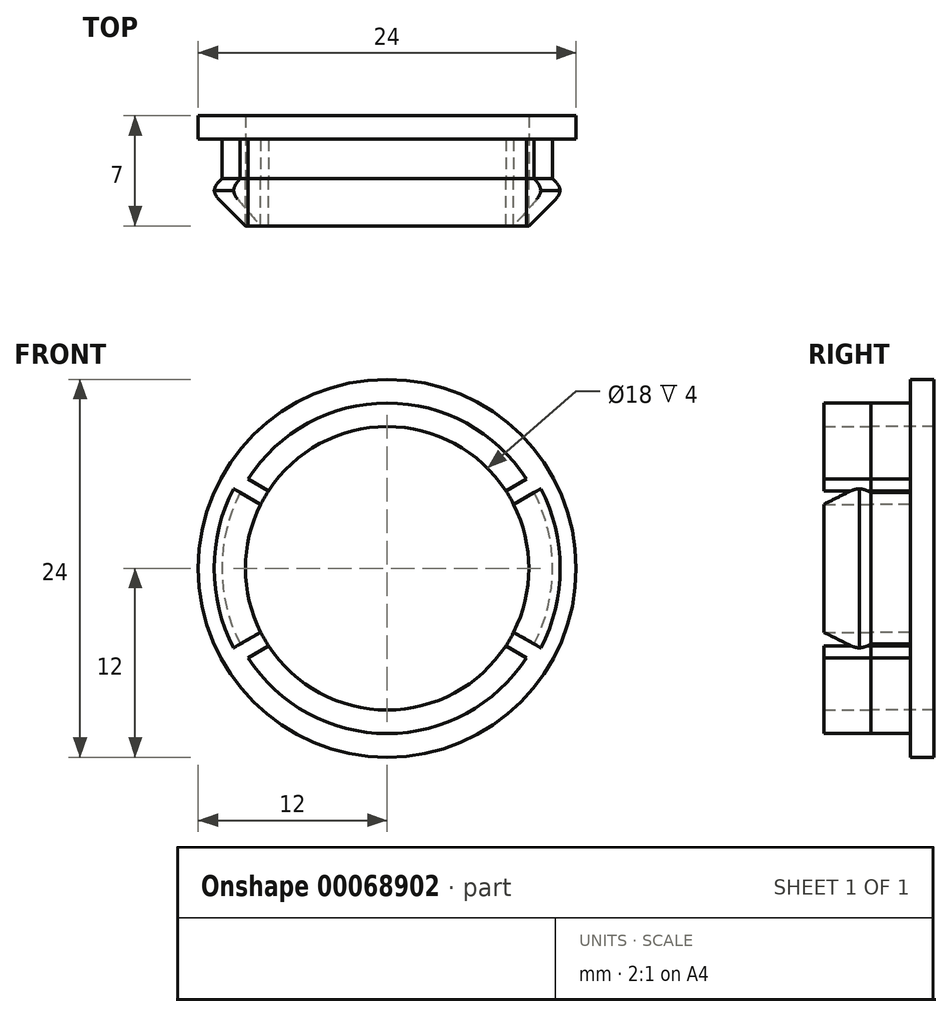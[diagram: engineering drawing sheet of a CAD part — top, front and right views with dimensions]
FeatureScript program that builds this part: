
annotation { "Feature Type Name" : "Feature", "Feature Type Description" : "" }
export const myFeature = defineFeature(function(context is Context, id is Id, definition is map)
    precondition{}
    {
        {
            var Q0;
            Q0=qCreatedBy(makeId("Front.planeOp"),FACE);
            var sketch = newSketch(context, id + "F0", { "sketchPlane" : qUnion([Q0])});
            skArc(sketch, "E0", {"start": v(-9.33, 4.81) * mm, "mid": v(-10.5, 0) * mm, "end": v(-9.33, -4.81) * mm});
            skArc(sketch, "E1.0", {"start": v(-8.03, 4.06) * mm, "mid": v(-9, 0) * mm, "end": v(-8.03, -4.06) * mm});
            skLineSegment(sketch, "E2", {"start": v(-12.74, 7.35) * mm, "end": v(0, 0) * mm, "construction": true});
            skLineSegment(sketch, "E3.MirrorCS", {"start": v(-12.74, -7.35) * mm, "end": v(0, 0) * mm, "construction": true});
            skLineSegment(sketch, "E4.0", {"start": v(-12.88, -6.86) * mm, "end": v(-1, 0) * mm});
            skLineSegment(sketch, "E4.1", {"start": v(-9.33, 4.81) * mm, "end": v(-1, 0) * mm});
            skLineSegment(sketch, "E5.0", {"start": v(-12.16, -7.6) * mm, "end": v(0, -0.58) * mm});
            skLineSegment(sketch, "E5.1", {"start": v(-8.83, 5.68) * mm, "end": v(0, 0.58) * mm});
            skLineSegment(sketch, "E6.MirrorCS", {"start": v(12.16, -7.6) * mm, "end": v(0, -0.58) * mm});
            skLineSegment(sketch, "E7.MirrorCS", {"start": v(12.74, 7.35) * mm, "end": v(0, 0) * mm, "construction": true});
            skLineSegment(sketch, "E8.MirrorCS", {"start": v(12.74, -7.35) * mm, "end": v(0, 0) * mm, "construction": true});
            skLineSegment(sketch, "E9.MirrorCS", {"start": v(12.88, -6.86) * mm, "end": v(1, 0) * mm});
            skLineSegment(sketch, "E10.MirrorCS", {"start": v(12.99, 6.92) * mm, "end": v(1, 0) * mm});
            skLineSegment(sketch, "E11.MirrorCS", {"start": v(12.49, 7.79) * mm, "end": v(0, 0.58) * mm});
            skPoint(sketch, "E12.orphan", {"position": v(-12.99, 6.92) * mm});
            skPoint(sketch, "E13.orphan", {"position": v(-12.49, 7.79) * mm});
            skPoint(sketch, "E14.orphan", {"position": v(1, 0) * mm});
            skPoint(sketch, "E15.trimOffspring.end.orphan", {"position": v(-1, 0) * mm});
            skArc(sketch, "E16.trimOffspring", {"start": v(7.53, 4.93) * mm, "mid": v(0, 9) * mm, "end": v(-7.53, 4.93) * mm});
            skArc(sketch, "E17.trimOffspring", {"start": v(8.83, 5.68) * mm, "mid": v(0, 10.5) * mm, "end": v(-8.83, 5.68) * mm});
            skArc(sketch, "E18.trimOffspring", {"start": v(8.03, -4.06) * mm, "mid": v(9, 0) * mm, "end": v(8.03, 4.06) * mm});
            skArc(sketch, "E19.trimOffspring", {"start": v(9.33, -4.81) * mm, "mid": v(10.5, 0) * mm, "end": v(9.33, 4.81) * mm});
            skArc(sketch, "E20.trimOffspring", {"start": v(-7.53, -4.93) * mm, "mid": v(0, -9) * mm, "end": v(7.53, -4.93) * mm});
            skArc(sketch, "E21.trimOffspring", {"start": v(-8.83, -5.68) * mm, "mid": v(0, -10.5) * mm, "end": v(8.83, -5.68) * mm});
            skSolve(sketch);
        }
        {
            var Q0;
            Q0=makeQuery(id+"F0.imprint","IMPRINT",FACE,{"disambiguationData":[TD([[makeQuery(id+"F0.imprint","IMPRINT",EDGE,{"derivedFrom":sQuery(id+"F0.wireOp",EDGE,"E0")}),1.0]])]});
            var Q1;
            {var subQ2=sQuery(id+"F0.wireOp",EDGE,"E16.trimOffspring");Q1=makeQuery(id+"F0.imprint","IMPRINT",FACE,{"disambiguationData":[TD([[makeQuery(id+"F0.imprint","IMPRINT",EDGE,{"derivedFrom":subQ2}),-1.0]])]});}
            var Q2;
            {var subQ0=sQuery(id+"F0.wireOp",EDGE,"E18.trimOffspring");Q2=makeQuery(id+"F0.imprint","IMPRINT",FACE,{"disambiguationData":[TD([[makeQuery(id+"F0.imprint","IMPRINT",EDGE,{"derivedFrom":subQ0}),-1.0]])]});}
            var Q3;
            {var subQ0=sQuery(id+"F0.wireOp",EDGE,"E20.trimOffspring");Q3=makeQuery(id+"F0.imprint","IMPRINT",FACE,{"disambiguationData":[TD([[makeQuery(id+"F0.imprint","IMPRINT",EDGE,{"derivedFrom":subQ0}),-1.0]])]});}
            extrude(context, id + "F1", {"entities" : qUnion([Q0, Q1, Q2, Q3]), "oppositeDirection" : true, "depth" : 2.5 * mm});
        }
        {
            var Q0;
            Q0=makeQuery(id+"F1.opExtrude","CAP_FACE",FACE,{"disambiguationData":[OSD([sQuery(id+"F0.wireOp",EDGE,"E0"),sQuery(id+"F0.wireOp",EDGE,"E1.0")])],"isStart":false});
            var sketch = newSketch(context, id + "F2", { "sketchPlane" : qUnion([Q0])});
            skCircle(sketch, "E22", {"center": v(0, 0) * mm, "radius": 12 * mm});
            skCircle(sketch, "E23", {"center": v(0, 0) * mm, "radius": 9 * mm});
            skSolve(sketch);
        }
        {
            var Q0;
            Q0=qSketchRegion(id+"F2",true);
            extrude(context, id + "F3", {"entities" : qUnion([Q0]), "operationType" : NewBodyOperationType.ADD, "depth" : 1.5 * mm});
        }
        {
            var Q0;
            {var subQ0=sQuery(id+"F0.wireOp",EDGE,"E0");Q0=makeQuery(id+"F0.imprint","IMPRINT",FACE,{"disambiguationData":[TD([[makeQuery(id+"F0.imprint","IMPRINT",EDGE,{"derivedFrom":subQ0}),1.0]])]});}
            var sketch = newSketch(context, id + "F4", { "sketchPlane" : qUnion([Q0])});
            skArc(sketch, "E24", {"start": v(7.53, 4.93) * mm, "mid": v(0, 9) * mm, "end": v(-7.53, 4.93) * mm});
            skArc(sketch, "E25", {"start": v(9.77, -5.06) * mm, "mid": v(11, 0) * mm, "end": v(9.77, 5.06) * mm});
            skLineSegment(sketch, "E26", {"start": v(0, 0) * mm, "end": v(-1, 0) * mm, "construction": true});
            skLineSegment(sketch, "E27", {"start": v(-1, 0) * mm, "end": v(-12.1, -6.4) * mm, "construction": true});
            skLineSegment(sketch, "E28.MirrorCS", {"start": v(1, 0) * mm, "end": v(12.1, -6.4) * mm, "construction": true});
            skLineSegment(sketch, "E29.MirrorCS", {"start": v(0, 0) * mm, "end": v(1, 0) * mm, "construction": true});
            skLineSegment(sketch, "E30.MirrorCS", {"start": v(-1, 0) * mm, "end": v(-12.1, 6.4) * mm, "construction": true});
            skLineSegment(sketch, "E31.MirrorCS", {"start": v(1, 0) * mm, "end": v(12.1, 6.4) * mm, "construction": true});
            skArc(sketch, "E32.trimOffspring", {"start": v(-9.77, 5.06) * mm, "mid": v(-11, 0) * mm, "end": v(-9.77, -5.06) * mm});
            skLineSegment(sketch, "E33", {"start": v(-9.77, 5.06) * mm, "end": v(-8.03, 4.06) * mm});
            skLineSegment(sketch, "E34", {"start": v(-9.77, -5.06) * mm, "end": v(-8.03, -4.06) * mm});
            skLineSegment(sketch, "E35", {"start": v(8.03, 4.06) * mm, "end": v(9.77, 5.06) * mm});
            skLineSegment(sketch, "E36", {"start": v(8.03, -4.06) * mm, "end": v(9.77, -5.06) * mm});
            skArc(sketch, "E37", {"start": v(-8.83, -5.68) * mm, "mid": v(0, -10.5) * mm, "end": v(8.83, -5.68) * mm});
            skArc(sketch, "E38.trimOffspring", {"start": v(8.83, 5.68) * mm, "mid": v(0, 10.5) * mm, "end": v(-8.83, 5.68) * mm});
            skLineSegment(sketch, "E39", {"start": v(0, 0) * mm, "end": v(0, -0.58) * mm, "construction": true});
            skLineSegment(sketch, "E40", {"start": v(-7.53, -4.93) * mm, "end": v(-8.83, -5.68) * mm});
            skLineSegment(sketch, "E41.MirrorCS", {"start": v(7.53, -4.93) * mm, "end": v(8.83, -5.68) * mm});
            skLineSegment(sketch, "E42.MirrorCS", {"start": v(-7.53, 4.93) * mm, "end": v(-8.83, 5.68) * mm});
            skLineSegment(sketch, "E43.MirrorCS", {"start": v(7.53, 4.93) * mm, "end": v(8.83, 5.68) * mm});
            skArc(sketch, "E44.trimOffspring", {"start": v(-8.03, 4.06) * mm, "mid": v(-9, 0) * mm, "end": v(-8.03, -4.06) * mm});
            skPoint(sketch, "E45.orphan", {"position": v(0, 0.58) * mm});
            skPoint(sketch, "E46.orphan", {"position": v(0, -0.58) * mm});
            skArc(sketch, "E47.trimOffspring", {"start": v(-7.53, -4.93) * mm, "mid": v(0, -9) * mm, "end": v(7.53, -4.93) * mm});
            skArc(sketch, "E48.trimOffspring", {"start": v(8.03, -4.06) * mm, "mid": v(9, 0) * mm, "end": v(8.03, 4.06) * mm});
            skSolve(sketch);
        }
        {
            var Q0;
            Q0=qSketchRegion(id+"F4",true);
            extrude(context, id + "F5", {"entities" : qUnion([Q0]), "depth" : 3 * mm});
        }
        {
            var Q0;
            Q0=makeQuery(id+"F5.opExtrude","CAP_EDGE",EDGE,{"disambiguationData":[OSD([sQuery(id+"F4.wireOp",EDGE,"E32.trimOffspring")])],"isStart":false});
            var Q1;
            Q1=makeQuery(id+"F5.opExtrude","CAP_EDGE",EDGE,{"disambiguationData":[OSD([sQuery(id+"F4.wireOp",EDGE,"E25")])],"isStart":false});
            chamfer(context, id + "F6", {"entities" : qUnion([Q0, Q1]), "width" : 2 * mm, "tangentPropagation" : true});
        }
        {
            var Q0;
            Q0=makeQuery(id+"F5.opExtrude","CAP_EDGE",EDGE,{"disambiguationData":[OSD([sQuery(id+"F4.wireOp",EDGE,"E32.trimOffspring")])],"isStart":true});
            var Q1;
            Q1=makeQuery(id+"F5.opExtrude","CAP_EDGE",EDGE,{"disambiguationData":[OSD([sQuery(id+"F4.wireOp",EDGE,"E25")])],"isStart":true});
            chamfer(context, id + "F7", {"entities" : qUnion([Q0, Q1]), "width" : 0.5 * mm, "tangentPropagation" : true});
        }
        {
            var Q0;
            {var subQ0=sQuery(id+"F4.wireOp",EDGE,"E32.trimOffspring");Q0=makeQuery(id+"F6.opChamfer","BLEND_EDGE",EDGE,{"blendedFrom":[makeQuery(id+"F5.opExtrude","CAP_EDGE",EDGE,{"disambiguationData":[OSD([subQ0])],"isStart":false}),makeQuery(id+"F5.opExtrude","SWEPT_FACE",FACE,{"disambiguationData":[OSD([subQ0])]})],"blendedInto":[makeQuery(id+"F5.opExtrude","SWEPT_FACE",FACE,{"disambiguationData":[OSD([subQ0])]})]});}
            var Q1;
            {var subQ0=sQuery(id+"F4.wireOp",EDGE,"E32.trimOffspring");Q1=makeQuery(id+"F7.opChamfer","BLEND_EDGE",EDGE,{"blendedFrom":[makeQuery(id+"F5.opExtrude","CAP_EDGE",EDGE,{"disambiguationData":[OSD([subQ0])],"isStart":true}),makeQuery(id+"F5.opExtrude","SWEPT_FACE",FACE,{"disambiguationData":[OSD([subQ0])]})],"blendedInto":[makeQuery(id+"F5.opExtrude","SWEPT_FACE",FACE,{"disambiguationData":[OSD([subQ0])]})]});}
            var Q2;
            {var subQ0=sQuery(id+"F4.wireOp",EDGE,"E25");Q2=makeQuery(id+"F6.opChamfer","BLEND_EDGE",EDGE,{"blendedFrom":[makeQuery(id+"F5.opExtrude","CAP_EDGE",EDGE,{"disambiguationData":[OSD([subQ0])],"isStart":false}),makeQuery(id+"F5.opExtrude","SWEPT_FACE",FACE,{"disambiguationData":[OSD([subQ0])]})],"blendedInto":[makeQuery(id+"F5.opExtrude","SWEPT_FACE",FACE,{"disambiguationData":[OSD([subQ0])]})]});}
            var Q3;
            {var subQ0=sQuery(id+"F4.wireOp",EDGE,"E25");Q3=makeQuery(id+"F7.opChamfer","BLEND_EDGE",EDGE,{"blendedFrom":[makeQuery(id+"F5.opExtrude","CAP_EDGE",EDGE,{"disambiguationData":[OSD([subQ0])],"isStart":true}),makeQuery(id+"F5.opExtrude","SWEPT_FACE",FACE,{"disambiguationData":[OSD([subQ0])]})],"blendedInto":[makeQuery(id+"F5.opExtrude","SWEPT_FACE",FACE,{"disambiguationData":[OSD([subQ0])]})]});}
            fillet(context, id + "F8", {"entities" : qUnion([Q0, Q1, Q2, Q3]), "radius" : 1 * mm, "tangentPropagation" : true, "allowEdgeOverflow" : false});
        }
    });
